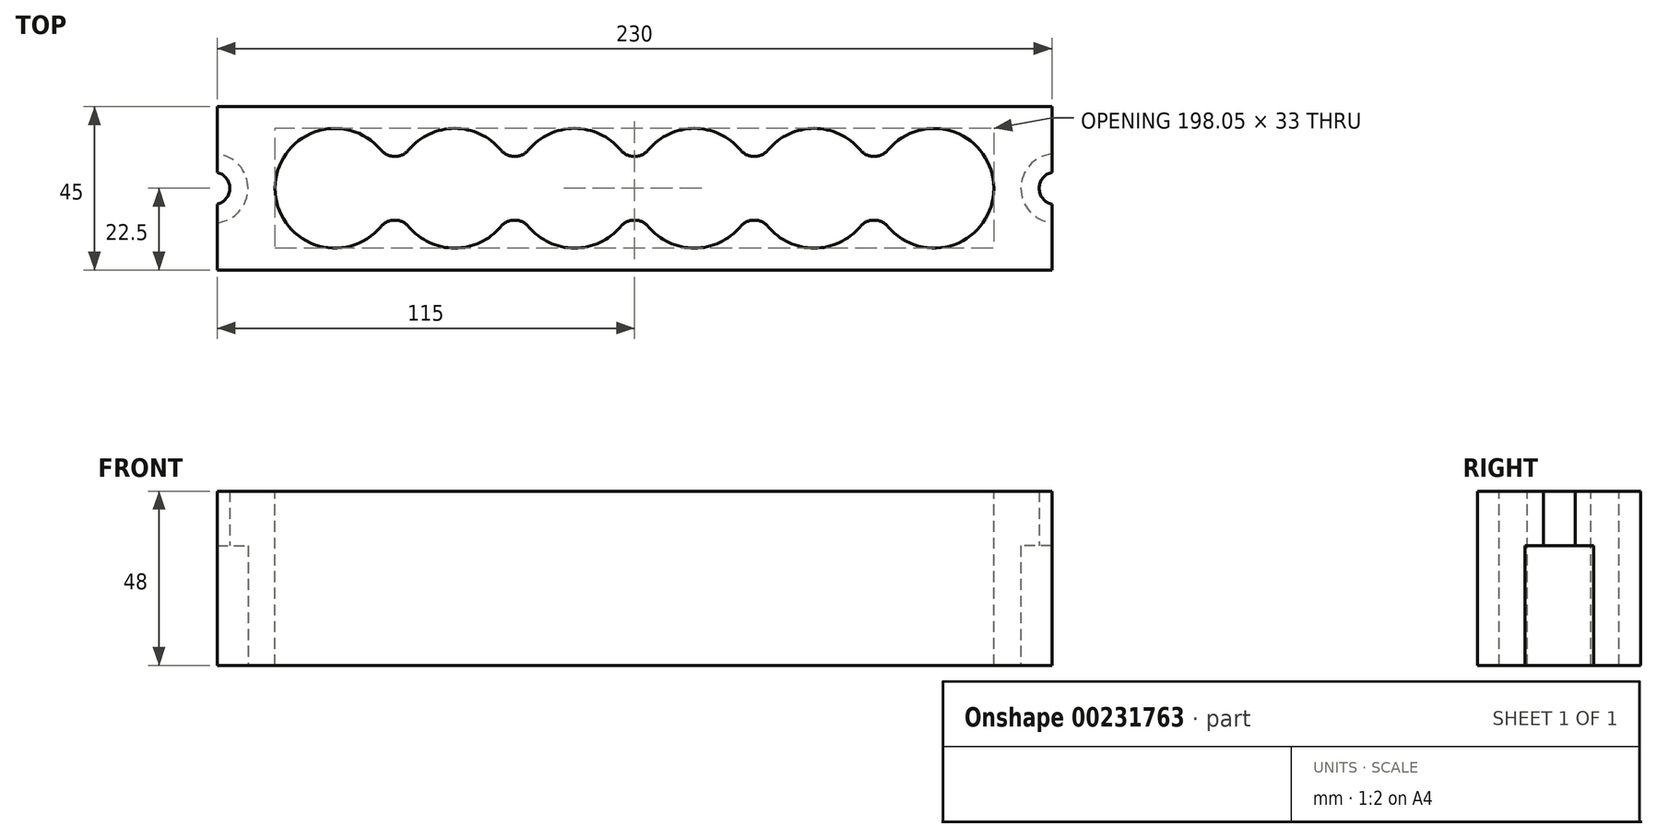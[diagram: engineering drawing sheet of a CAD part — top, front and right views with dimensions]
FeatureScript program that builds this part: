
annotation { "Feature Type Name" : "Feature", "Feature Type Description" : "" }
export const myFeature = defineFeature(function(context is Context, id is Id, definition is map)
    precondition{}
    {
        {
            var Q0;
            Q0=qCreatedBy(makeId("Top.planeOp"),FACE);
            var sketch = newSketch(context, id + "F0", { "sketchPlane" : qUnion([Q0])});
            skLineSegment(sketch, "E0.bottom", {"start": v(115, 22.5) * mm, "end": v(-115, 22.5) * mm});
            skLineSegment(sketch, "E0.top", {"start": v(115, -22.5) * mm, "end": v(-115, -22.5) * mm});
            skLineSegment(sketch, "E0.left", {"start": v(115, 22.5) * mm, "end": v(115, -22.5) * mm});
            skLineSegment(sketch, "E0.right", {"start": v(-115, 22.5) * mm, "end": v(-115, -22.5) * mm});
            skPoint(sketch, "E0.middle", {"position": v(0, 0) * mm});
            skSolve(sketch);
        }
        {
            var Q0;
            Q0=makeQuery(id+"F0.imprint","IMPRINT",FACE,{"disambiguationData":[TD([[makeQuery(id+"F0.imprint","IMPRINT",EDGE,{"derivedFrom":sQuery(id+"F0.wireOp",EDGE,"E0.bottom")}),1.0]])]});
            extrude(context, id + "F1", {"entities" : qUnion([Q0]), "depth" : 48 * mm});
        }
        {
            var Q0;
            Q0=makeQuery(id+"F1.opExtrude","CAP_FACE",FACE,{"disambiguationData":[OSD([sQuery(id+"F0.wireOp",EDGE,"E0.bottom"),sQuery(id+"F0.wireOp",EDGE,"E0.top"),sQuery(id+"F0.wireOp",EDGE,"E0.left"),sQuery(id+"F0.wireOp",EDGE,"E0.right")])],"isStart":false});
            var sketch = newSketch(context, id + "F2", { "sketchPlane" : qUnion([Q0])});
            skLineSegment(sketch, "E1.direction1", {"start": v(-82.52, 0) * mm, "end": v(-49.51, 0) * mm, "construction": true});
            skLineSegment(sketch, "E2", {"start": v(-115, 0) * mm, "end": v(-99.02, 0) * mm, "construction": true});
            skLineSegment(sketch, "E3", {"start": v(115, 0) * mm, "end": v(99.03, 0) * mm, "construction": true});
            skArc(sketch, "E4", {"start": v(-99.02, 0) * mm, "mid": v(-88.15, -15.51) * mm, "end": v(-69.86, -10.57) * mm});
            skArc(sketch, "E5", {"start": v(-69.86, 10.57) * mm, "mid": v(-88.15, 15.51) * mm, "end": v(-99.02, 0) * mm});
            skLineSegment(sketch, "E6", {"start": v(-99.03, 0) * mm, "end": v(99.03, 0) * mm, "construction": true});
            skArc(sketch, "E7", {"start": v(-62.18, -10.57) * mm, "mid": v(-49.51, -16.5) * mm, "end": v(-36.85, -10.57) * mm});
            skArc(sketch, "E8", {"start": v(-36.85, 10.57) * mm, "mid": v(-49.51, 16.5) * mm, "end": v(-62.18, 10.57) * mm});
            skArc(sketch, "E9", {"start": v(-29.17, -10.57) * mm, "mid": v(-16.5, -16.5) * mm, "end": v(-3.84, -10.57) * mm});
            skArc(sketch, "E10", {"start": v(-3.84, 10.57) * mm, "mid": v(-16.5, 16.5) * mm, "end": v(-29.17, 10.57) * mm});
            skArc(sketch, "E11", {"start": v(3.84, -10.57) * mm, "mid": v(16.5, -16.5) * mm, "end": v(29.17, -10.57) * mm});
            skArc(sketch, "E12", {"start": v(29.17, 10.57) * mm, "mid": v(16.5, 16.5) * mm, "end": v(3.84, 10.57) * mm});
            skArc(sketch, "E13", {"start": v(36.85, -10.57) * mm, "mid": v(49.52, -16.5) * mm, "end": v(62.18, -10.57) * mm});
            skArc(sketch, "E14", {"start": v(62.18, 10.57) * mm, "mid": v(49.51, 16.5) * mm, "end": v(36.85, 10.57) * mm});
            skArc(sketch, "E15", {"start": v(69.86, -10.57) * mm, "mid": v(88.15, -15.51) * mm, "end": v(99.03, 0) * mm});
            skArc(sketch, "E16", {"start": v(99.03, 0) * mm, "mid": v(88.15, 15.51) * mm, "end": v(69.86, 10.57) * mm});
            skArc(sketch, "E17.filletArc", {"start": v(-69.86, 10.57) * mm, "mid": v(-66.02, 8.78) * mm, "end": v(-62.18, 10.57) * mm});
            skArc(sketch, "E18.filletArc", {"start": v(-62.18, -10.57) * mm, "mid": v(-66.02, -8.78) * mm, "end": v(-69.86, -10.57) * mm});
            skArc(sketch, "E19.filletArc", {"start": v(-29.17, -10.57) * mm, "mid": v(-33, -8.78) * mm, "end": v(-36.85, -10.57) * mm});
            skArc(sketch, "E20.filletArc", {"start": v(-36.85, 10.57) * mm, "mid": v(-33, 8.78) * mm, "end": v(-29.17, 10.57) * mm});
            skArc(sketch, "E21.filletArc", {"start": v(-3.84, 10.57) * mm, "mid": v(0, 8.78) * mm, "end": v(3.84, 10.57) * mm});
            skArc(sketch, "E22.filletArc", {"start": v(3.84, -10.57) * mm, "mid": v(0, -8.78) * mm, "end": v(-3.84, -10.57) * mm});
            skArc(sketch, "E23.filletArc", {"start": v(36.85, -10.57) * mm, "mid": v(33.01, -8.78) * mm, "end": v(29.17, -10.57) * mm});
            skArc(sketch, "E24.filletArc", {"start": v(29.17, 10.57) * mm, "mid": v(33.01, 8.78) * mm, "end": v(36.85, 10.57) * mm});
            skArc(sketch, "E25.filletArc", {"start": v(62.18, 10.57) * mm, "mid": v(66.02, 8.78) * mm, "end": v(69.86, 10.57) * mm});
            skArc(sketch, "E26.filletArc", {"start": v(69.86, -10.57) * mm, "mid": v(66.02, -8.78) * mm, "end": v(62.18, -10.57) * mm});
            skSolve(sketch);
        }
        {
            var Q0;
            Q0=makeQuery(id+"F2.imprint","IMPRINT",FACE,{"disambiguationData":[TD([[makeQuery(id+"F2.imprint","IMPRINT",EDGE,{"derivedFrom":sQuery(id+"F2.wireOp",EDGE,"E4")}),1.0]])]});
            var Q1;
            Q1=makeQuery(id+"F1.opExtrude","CAP_FACE",FACE,{"disambiguationData":[OSD([sQuery(id+"F0.wireOp",EDGE,"E0.bottom"),sQuery(id+"F0.wireOp",EDGE,"E0.top"),sQuery(id+"F0.wireOp",EDGE,"E0.left"),sQuery(id+"F0.wireOp",EDGE,"E0.right")])],"isStart":true});
            extrude(context, id + "F3", {"entities" : qUnion([Q0]), "operationType" : NewBodyOperationType.REMOVE, "endBound" : BoundingType.UP_TO_SURFACE, "oppositeDirection" : true, "endBoundEntityFace" : qUnion([Q1]), "depth" : 25 * mm});
        }
        {
            var Q0;
            Q0=makeQuery(id+"F1.opExtrude","CAP_FACE",FACE,{"disambiguationData":[OSD([sQuery(id+"F0.wireOp",EDGE,"E0.bottom"),sQuery(id+"F0.wireOp",EDGE,"E0.top"),sQuery(id+"F0.wireOp",EDGE,"E0.left"),sQuery(id+"F0.wireOp",EDGE,"E0.right")])],"isStart":true});
            var sketch = newSketch(context, id + "F4", { "sketchPlane" : qUnion([Q0])});
            skLineSegment(sketch, "E27", {"start": v(-116, 9.53) * mm, "end": v(-115, 9.53) * mm});
            skArc(sketch, "E28", {"start": v(-116, 9.53) * mm, "mid": v(-106.47, 0) * mm, "end": v(-116, -9.53) * mm});
            skLineSegment(sketch, "E29", {"start": v(-115, -9.53) * mm, "end": v(-116, -9.53) * mm});
            skLineSegment(sketch, "E30.MirrorCS", {"start": v(116, 9.53) * mm, "end": v(115, 9.53) * mm});
            skArc(sketch, "E31.MirrorCS", {"start": v(116, 9.53) * mm, "mid": v(106.47, 0) * mm, "end": v(116, -9.53) * mm});
            skLineSegment(sketch, "E32.MirrorCS", {"start": v(115, -9.53) * mm, "end": v(116, -9.53) * mm});
            skLineSegment(sketch, "E33", {"start": v(-115, 9.53) * mm, "end": v(-115, -9.53) * mm});
            skLineSegment(sketch, "E34", {"start": v(115, 9.53) * mm, "end": v(115, -9.52) * mm});
            skSolve(sketch);
        }
        {
            var Q0;
            Q0 = qSketchRegion(id + "F4", true);
            var Q1;
            Q1=makeQuery(id+"F1.opExtrude","CAP_FACE",FACE,{"disambiguationData":[OSD([sQuery(id+"F0.wireOp",EDGE,"E0.bottom"),sQuery(id+"F0.wireOp",EDGE,"E0.top"),sQuery(id+"F0.wireOp",EDGE,"E0.left"),sQuery(id+"F0.wireOp",EDGE,"E0.right")])],"isStart":false});
            extrude(context, id + "F5", {"entities" : qUnion([Q0]), "operationType" : NewBodyOperationType.REMOVE, "oppositeDirection" : true, "endBoundEntityFace" : qUnion([Q1]), "depth" : 33 * mm});
        }
        {
            var Q0;
            Q0=makeQuery(id+"F5.boolean.opBoolean","COPY",FACE,{"derivedFrom":makeQuery(id+"F5.opExtrude","CAP_FACE",FACE,{"disambiguationData":[OSD([sQuery(id+"F4.wireOp",EDGE,"E28"),sQuery(id+"F4.wireOp",EDGE,"E33")])],"isStart":false})});
            var sketch = newSketch(context, id + "F6", { "sketchPlane" : qUnion([Q0])});
            skLineSegment(sketch, "E35.0", {"start": v(115, 22.5) * mm, "end": v(-115, 22.5) * mm});
            skLineSegment(sketch, "E36.0", {"start": v(115, -22.5) * mm, "end": v(-115, -22.5) * mm});
            skCircle(sketch, "E37", {"center": v(-116, 0) * mm, "radius": 4.5 * mm});
            skCircle(sketch, "E38.MirrorC", {"center": v(116, 0) * mm, "radius": 4.5 * mm});
            skSolve(sketch);
        }
        {
            var Q0;
            Q0 = qSketchRegion(id + "F6", true);
            var Q1;
            Q1=makeQuery(id+"F1.opExtrude","CAP_FACE",FACE,{"disambiguationData":[OSD([sQuery(id+"F0.wireOp",EDGE,"E0.bottom"),sQuery(id+"F0.wireOp",EDGE,"E0.top"),sQuery(id+"F0.wireOp",EDGE,"E0.left"),sQuery(id+"F0.wireOp",EDGE,"E0.right")])],"isStart":false});
            extrude(context, id + "F7", {"entities" : qUnion([Q0]), "operationType" : NewBodyOperationType.REMOVE, "endBound" : BoundingType.UP_TO_SURFACE, "oppositeDirection" : true, "endBoundEntityFace" : qUnion([Q1]), "depth" : 25 * mm});
        }
    });
